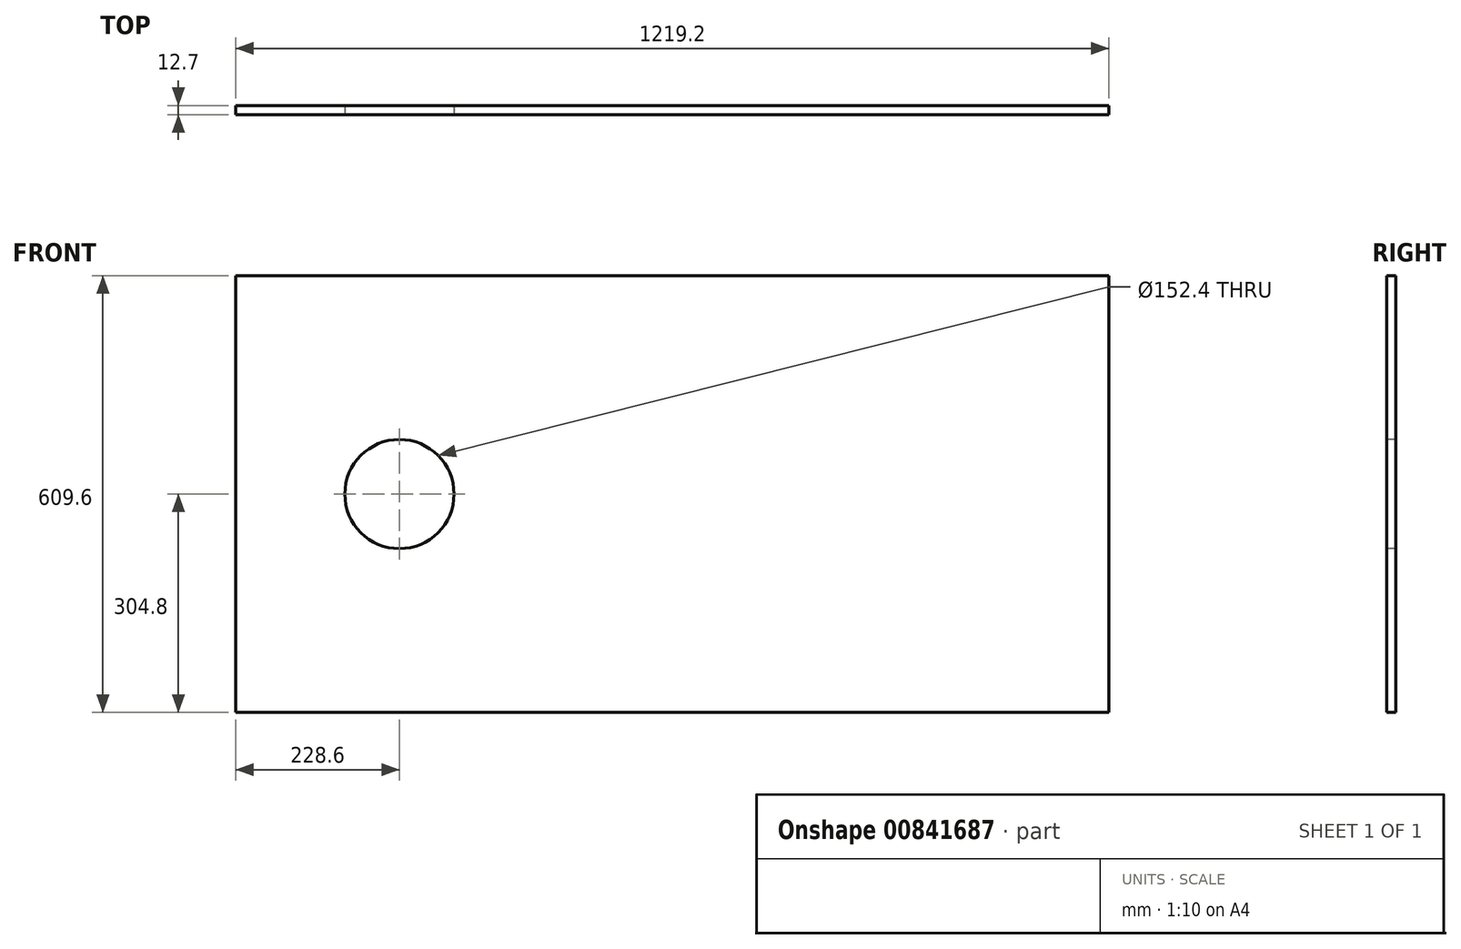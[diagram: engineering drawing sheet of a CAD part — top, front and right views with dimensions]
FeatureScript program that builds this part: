
annotation { "Feature Type Name" : "Feature", "Feature Type Description" : "" }
export const myFeature = defineFeature(function(context is Context, id is Id, definition is map)
    precondition{}
    {
        {
            var Q0;
            Q0=qCreatedBy(makeId("Front.planeOp"),FACE);
            var sketch = newSketch(context, id + "F0", { "sketchPlane" : qUnion([Q0])});
            skLineSegment(sketch, "E0.bottom", {"start": v(609.6, -304.8) * mm, "end": v(-609.6, -304.8) * mm});
            skLineSegment(sketch, "E0.top", {"start": v(609.6, 304.8) * mm, "end": v(-609.6, 304.8) * mm});
            skLineSegment(sketch, "E0.left", {"start": v(609.6, -304.8) * mm, "end": v(609.6, 304.8) * mm});
            skLineSegment(sketch, "E0.right", {"start": v(-609.6, -304.8) * mm, "end": v(-609.6, 304.8) * mm});
            skPoint(sketch, "E0.middle", {"position": v(0, 0) * mm});
            skSolve(sketch);
        }
        {
            var Q0;
            Q0 = qSketchRegion(id + "F0", true);
            extrude(context, id + "F1", {"entities" : qUnion([Q0]), "depth" : 12.7 * mm, "offsetDistance" : 25.4 * mm});
        }
        {
            var Q0;
            Q0=makeQuery(id+"F1.opExtrude","CAP_FACE",FACE,{"disambiguationData":[OSD([sQuery(id+"F0.wireOp",EDGE,"E0.bottom"),sQuery(id+"F0.wireOp",EDGE,"E0.top"),sQuery(id+"F0.wireOp",EDGE,"E0.left"),sQuery(id+"F0.wireOp",EDGE,"E0.right")])],"isStart":false});
            var sketch = newSketch(context, id + "F2", { "sketchPlane" : qUnion([Q0])});
            skLineSegment(sketch, "E1", {"start": v(-381, 304.8) * mm, "end": v(-381, -304.8) * mm, "construction": true});
            skPoint(sketch, "E2", {"position": v(-381, 0) * mm});
            skSolve(sketch);
        }
        {
            var Q0;
            Q0=sQuery(id+"F2.wireOp",VERTEX,"E2");
            var Q1;
            Q1=makeQuery(id+"F1.opExtrude","SWEPT_BODY",BODY,{"disambiguationData":[OSD([sQuery(id+"F0.wireOp",EDGE,"E0.bottom"),sQuery(id+"F0.wireOp",EDGE,"E0.top"),sQuery(id+"F0.wireOp",EDGE,"E0.left"),sQuery(id+"F0.wireOp",EDGE,"E0.right")])]});
            hole(context, id + "F3", {"style" : HoleStyle.SIMPLE, "endStyle" : HoleEndStyle.THROUGH, "holeDiameter" : 152.4 * mm, "majorDiameter" : 6.35 * mm, "isTappedThrough" : true, "tappedDepth" : 12.7 * mm, "tapClearance" : 3, "locations" : qUnion([Q0]), "scope" : qUnion([Q1])});
        }
    });
